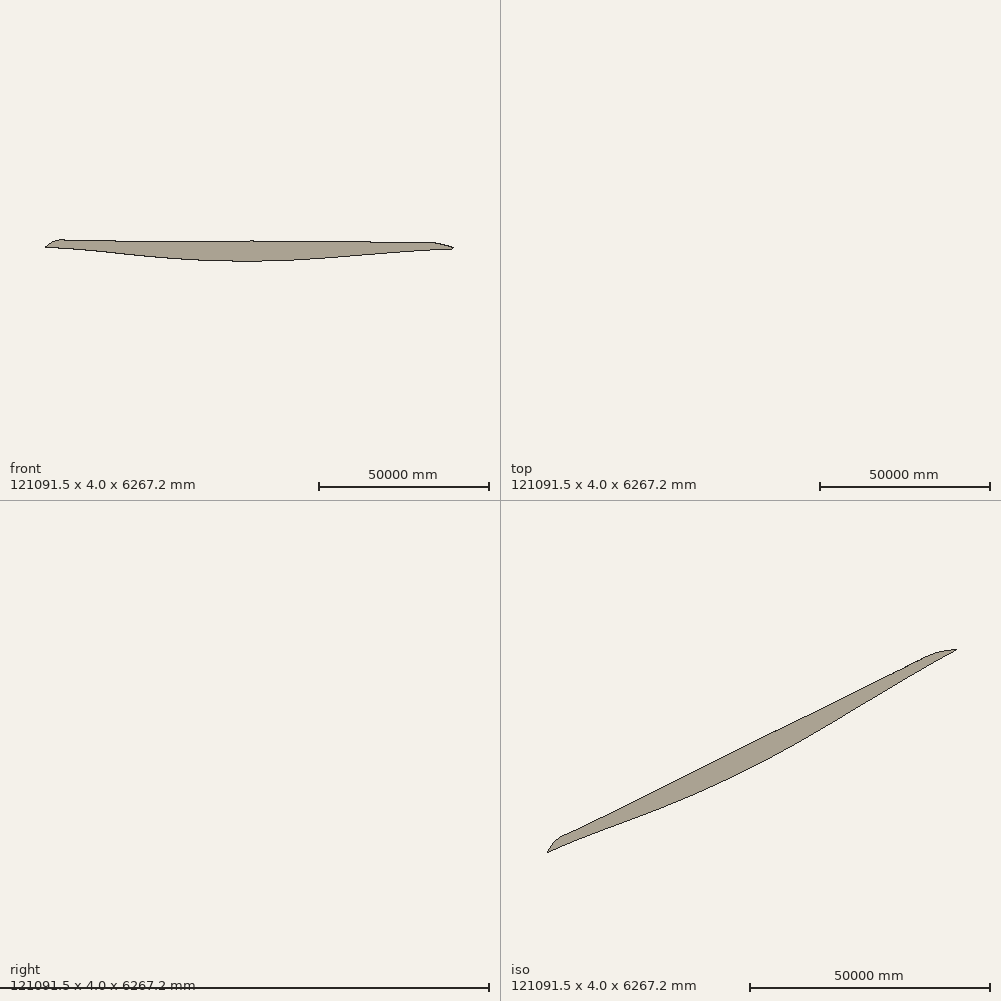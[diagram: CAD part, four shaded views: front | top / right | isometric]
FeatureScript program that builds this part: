
annotation { "Feature Type Name" : "Feature", "Feature Type Description" : "" }
export const myFeature = defineFeature(function(context is Context, id is Id, definition is map)
    precondition{}
    {
        {
            var Q0;
            Q0=qCreatedBy(makeId("Front.planeOp"),FACE);
            var sketch = newSketch(context, id + "F0", { "sketchPlane" : qUnion([Q0])});
            skLineSegment(sketch, "E0", {"start": v(45045.26, 2481.75) * mm, "end": v(45048.8, 2354.8) * mm});
            skLineSegment(sketch, "E1", {"start": v(45048.8, 2354.8) * mm, "end": v(45045.26, 2481.75) * mm});
            skLineSegment(sketch, "E2", {"start": v(45045.26, 2481.75) * mm, "end": v(46150.6, 2484.8) * mm});
            skLineSegment(sketch, "E3", {"start": v(46150.6, 2484.8) * mm, "end": v(46853.03, 2491.6) * mm});
            skLineSegment(sketch, "E4", {"start": v(46853.03, 2491.6) * mm, "end": v(47555.47, 2496.48) * mm});
            skLineSegment(sketch, "E5", {"start": v(47555.47, 2496.48) * mm, "end": v(48440.73, 2492.2) * mm});
            skLineSegment(sketch, "E6", {"start": v(48440.73, 2492.2) * mm, "end": v(49326.03, 2484.26) * mm});
            skLineSegment(sketch, "E7", {"start": v(49326.03, 2484.26) * mm, "end": v(49919.8, 2482.53) * mm});
            skLineSegment(sketch, "E8", {"start": v(49919.8, 2482.53) * mm, "end": v(50513.65, 2486.3) * mm});
            skLineSegment(sketch, "E9", {"start": v(50513.65, 2486.3) * mm, "end": v(51092.21, 2493.99) * mm});
            skLineSegment(sketch, "E10", {"start": v(51092.21, 2493.99) * mm, "end": v(51670.65, 2492.54) * mm});
            skLineSegment(sketch, "E11", {"start": v(51670.65, 2492.54) * mm, "end": v(52134.05, 2476.26) * mm});
            skLineSegment(sketch, "E12", {"start": v(52134.05, 2476.26) * mm, "end": v(52597.09, 2449.36) * mm});
            skLineSegment(sketch, "E13", {"start": v(52597.09, 2449.36) * mm, "end": v(52942.38, 2424.85) * mm});
            skLineSegment(sketch, "E14", {"start": v(52942.38, 2424.85) * mm, "end": v(53287.1, 2394.75) * mm});
            skLineSegment(sketch, "E15", {"start": v(53287.1, 2394.75) * mm, "end": v(53695.08, 2350.15) * mm});
            skLineSegment(sketch, "E16", {"start": v(53695.08, 2350.15) * mm, "end": v(54102.83, 2301.96) * mm});
            skLineSegment(sketch, "E17", {"start": v(54102.83, 2301.96) * mm, "end": v(54430.4, 2263.56) * mm});
            skLineSegment(sketch, "E18", {"start": v(54430.4, 2263.56) * mm, "end": v(54756.52, 2216.5) * mm});
            skLineSegment(sketch, "E19", {"start": v(54756.52, 2216.5) * mm, "end": v(55127.97, 2142.43) * mm});
            skLineSegment(sketch, "E20", {"start": v(55127.97, 2142.43) * mm, "end": v(55497.8, 2058.7) * mm});
            skLineSegment(sketch, "E21", {"start": v(55497.8, 2058.7) * mm, "end": v(55875.09, 1976.62) * mm});
            skLineSegment(sketch, "E22", {"start": v(55875.09, 1976.62) * mm, "end": v(56251.8, 1892.36) * mm});
            skLineSegment(sketch, "E23", {"start": v(56251.8, 1892.36) * mm, "end": v(56457.28, 1842.43) * mm});
            skLineSegment(sketch, "E24", {"start": v(56457.28, 1842.43) * mm, "end": v(56922.02, 1738.62) * mm});
            skLineSegment(sketch, "E25", {"start": v(56922.02, 1738.62) * mm, "end": v(57497.2, 1602.22) * mm});
            skLineSegment(sketch, "E26", {"start": v(57497.2, 1602.22) * mm, "end": v(57794.82, 1520.66) * mm});
            skLineSegment(sketch, "E27", {"start": v(57794.82, 1520.66) * mm, "end": v(58090.22, 1431.35) * mm});
            skLineSegment(sketch, "E28", {"start": v(58090.22, 1431.35) * mm, "end": v(58603.02, 1261.35) * mm});
            skLineSegment(sketch, "E29", {"start": v(58603.02, 1261.35) * mm, "end": v(59086.76, 1091.73) * mm});
            skLineSegment(sketch, "E30", {"start": v(59086.76, 1091.73) * mm, "end": v(59492.98, 946.42) * mm});
            skLineSegment(sketch, "E31", {"start": v(59492.98, 946.42) * mm, "end": v(59938.37, 778.4) * mm});
            skLineSegment(sketch, "E32", {"start": v(59938.37, 778.4) * mm, "end": v(60124.66, 698.72) * mm});
            skLineSegment(sketch, "E33", {"start": v(60124.66, 698.72) * mm, "end": v(60307.18, 610.96) * mm});
            skLineSegment(sketch, "E34", {"start": v(60307.18, 610.96) * mm, "end": v(60545.74, 477.23) * mm});
            skLineSegment(sketch, "E35", {"start": v(60545.74, 477.23) * mm, "end": v(60142.23, 460.8) * mm});
            skLineSegment(sketch, "E36", {"start": v(60142.23, 460.8) * mm, "end": v(59445.87, 431.56) * mm});
            skLineSegment(sketch, "E37", {"start": v(59445.87, 431.56) * mm, "end": v(58749.32, 407.68) * mm});
            skLineSegment(sketch, "E38", {"start": v(58749.32, 407.68) * mm, "end": v(58331.21, 398.44) * mm});
            skLineSegment(sketch, "E39", {"start": v(58331.21, 398.44) * mm, "end": v(57913.16, 387.67) * mm});
            skLineSegment(sketch, "E40", {"start": v(57913.16, 387.67) * mm, "end": v(57073.43, 348.12) * mm});
            skLineSegment(sketch, "E41", {"start": v(57073.43, 348.12) * mm, "end": v(56233.89, 305.57) * mm});
            skLineSegment(sketch, "E42", {"start": v(56233.89, 305.57) * mm, "end": v(55753.85, 287.64) * mm});
            skLineSegment(sketch, "E43", {"start": v(55753.85, 287.64) * mm, "end": v(54874.73, 250.05) * mm});
            skLineSegment(sketch, "E44", {"start": v(54874.73, 250.05) * mm, "end": v(53996, 204.36) * mm});
            skLineSegment(sketch, "E45", {"start": v(53996, 204.36) * mm, "end": v(52751.7, 129.04) * mm});
            skLineSegment(sketch, "E46", {"start": v(52751.7, 129.04) * mm, "end": v(51381.27, 28.51) * mm});
            skLineSegment(sketch, "E47", {"start": v(51381.27, 28.51) * mm, "end": v(50659.65, -10.07) * mm});
            skLineSegment(sketch, "E48", {"start": v(50659.65, -10.07) * mm, "end": v(49938.77, -59.86) * mm});
            skLineSegment(sketch, "E49", {"start": v(49938.77, -59.86) * mm, "end": v(49309.13, -95.03) * mm});
            skLineSegment(sketch, "E50", {"start": v(49309.13, -95.03) * mm, "end": v(48679.37, -128.4) * mm});
            skLineSegment(sketch, "E51", {"start": v(48679.37, -128.4) * mm, "end": v(48018.59, -172.58) * mm});
            skLineSegment(sketch, "E52", {"start": v(48018.59, -172.58) * mm, "end": v(47358.21, -223.25) * mm});
            skLineSegment(sketch, "E53", {"start": v(47358.21, -223.25) * mm, "end": v(46327.99, -299.15) * mm});
            skLineSegment(sketch, "E54", {"start": v(46327.99, -299.15) * mm, "end": v(45952.1, -322.03) * mm});
            skLineSegment(sketch, "E55", {"start": v(45952.1, -322.03) * mm, "end": v(45576.4, -347.4) * mm});
            skLineSegment(sketch, "E56", {"start": v(45576.4, -347.4) * mm, "end": v(45045.26, -395.72) * mm});
            skLineSegment(sketch, "E57", {"start": v(45045.26, -395.72) * mm, "end": v(45033.76, -269.23) * mm});
            skLineSegment(sketch, "E58", {"start": v(45033.76, -269.23) * mm, "end": v(45045.26, -395.72) * mm});
            skLineSegment(sketch, "E59", {"start": v(45045.26, -395.72) * mm, "end": v(43527.08, -510.83) * mm});
            skLineSegment(sketch, "E60", {"start": v(43527.08, -510.83) * mm, "end": v(41972.2, -629.35) * mm});
            skLineSegment(sketch, "E61", {"start": v(41972.2, -629.35) * mm, "end": v(39742.22, -806.31) * mm});
            skLineSegment(sketch, "E62", {"start": v(39742.22, -806.31) * mm, "end": v(37160.87, -1010) * mm});
            skLineSegment(sketch, "E63", {"start": v(37160.87, -1010) * mm, "end": v(34378.68, -1226.8) * mm});
            skLineSegment(sketch, "E64", {"start": v(34378.68, -1226.8) * mm, "end": v(31538.63, -1451.01) * mm});
            skLineSegment(sketch, "E65", {"start": v(31538.63, -1451.01) * mm, "end": v(30380.85, -1549.03) * mm});
            skLineSegment(sketch, "E66", {"start": v(30380.85, -1549.03) * mm, "end": v(29759.62, -1605.47) * mm});
            skLineSegment(sketch, "E67", {"start": v(29759.62, -1605.47) * mm, "end": v(29138.18, -1659.65) * mm});
            skLineSegment(sketch, "E68", {"start": v(29138.18, -1659.65) * mm, "end": v(28532.24, -1706.64) * mm});
            skLineSegment(sketch, "E69", {"start": v(28532.24, -1706.64) * mm, "end": v(27926.32, -1754.06) * mm});
            skLineSegment(sketch, "E70", {"start": v(27926.32, -1754.06) * mm, "end": v(27147.99, -1823.7) * mm});
            skLineSegment(sketch, "E71", {"start": v(27147.99, -1823.7) * mm, "end": v(26369.6, -1892.52) * mm});
            skLineSegment(sketch, "E72", {"start": v(26369.6, -1892.52) * mm, "end": v(25837.45, -1932.75) * mm});
            skLineSegment(sketch, "E73", {"start": v(25837.45, -1932.75) * mm, "end": v(25305.12, -1970.8) * mm});
            skLineSegment(sketch, "E74", {"start": v(25305.12, -1970.8) * mm, "end": v(24325.6, -2049.34) * mm});
            skLineSegment(sketch, "E75", {"start": v(24325.6, -2049.34) * mm, "end": v(23610.6, -2114.97) * mm});
            skLineSegment(sketch, "E76", {"start": v(23610.6, -2114.97) * mm, "end": v(22894.99, -2171.1) * mm});
            skLineSegment(sketch, "E77", {"start": v(22894.99, -2171.1) * mm, "end": v(22494.02, -2192.9) * mm});
            skLineSegment(sketch, "E78", {"start": v(22494.02, -2192.9) * mm, "end": v(22093, -2214.05) * mm});
            skLineSegment(sketch, "E79", {"start": v(22093, -2214.05) * mm, "end": v(21438.48, -2260.84) * mm});
            skLineSegment(sketch, "E80", {"start": v(21438.48, -2260.84) * mm, "end": v(21429.4, -2134.17) * mm});
            skLineSegment(sketch, "E81", {"start": v(21429.4, -2134.17) * mm, "end": v(21438.48, -2260.84) * mm});
            skLineSegment(sketch, "E82", {"start": v(21438.48, -2260.84) * mm, "end": v(20058.11, -2364.78) * mm});
            skLineSegment(sketch, "E83", {"start": v(20058.11, -2364.78) * mm, "end": v(18937.92, -2436.89) * mm});
            skLineSegment(sketch, "E84", {"start": v(18937.92, -2436.89) * mm, "end": v(17817.48, -2505.27) * mm});
            skLineSegment(sketch, "E85", {"start": v(17817.48, -2505.27) * mm, "end": v(16514.46, -2589.67) * mm});
            skLineSegment(sketch, "E86", {"start": v(16514.46, -2589.67) * mm, "end": v(15211.54, -2676.26) * mm});
            skLineSegment(sketch, "E87", {"start": v(15211.54, -2676.26) * mm, "end": v(13451.6, -2785.12) * mm});
            skLineSegment(sketch, "E88", {"start": v(13451.6, -2785.12) * mm, "end": v(11690.44, -2868.87) * mm});
            skLineSegment(sketch, "E89", {"start": v(11690.44, -2868.87) * mm, "end": v(10862.63, -2896.15) * mm});
            skLineSegment(sketch, "E90", {"start": v(10862.63, -2896.15) * mm, "end": v(10034.74, -2922) * mm});
            skLineSegment(sketch, "E91", {"start": v(10034.74, -2922) * mm, "end": v(8682.19, -2973.67) * mm});
            skLineSegment(sketch, "E92", {"start": v(8682.19, -2973.67) * mm, "end": v(7329.74, -3027.67) * mm});
            skLineSegment(sketch, "E93", {"start": v(7329.74, -3027.67) * mm, "end": v(5977.04, -3068.9) * mm});
            skLineSegment(sketch, "E94", {"start": v(5977.04, -3068.9) * mm, "end": v(4581.82, -3088.75) * mm});
            skLineSegment(sketch, "E95", {"start": v(4581.82, -3088.75) * mm, "end": v(3186.37, -3103.26) * mm});
            skLineSegment(sketch, "E96", {"start": v(3186.37, -3103.26) * mm, "end": v(1934.83, -3124.24) * mm});
            skLineSegment(sketch, "E97", {"start": v(1934.83, -3124.24) * mm, "end": v(683.35, -3133.59) * mm});
            skLineSegment(sketch, "E98", {"start": v(683.35, -3133.59) * mm, "end": v(110.99, -3127.46) * mm});
            skLineSegment(sketch, "E99", {"start": v(110.99, -3127.46) * mm, "end": v(-461.33, -3115.55) * mm});
            skLineSegment(sketch, "E100", {"start": v(-461.33, -3115.55) * mm, "end": v(-458.69, -2988.58) * mm});
            skLineSegment(sketch, "E101", {"start": v(-458.69, -2988.58) * mm, "end": v(-461.33, -3115.55) * mm});
            skLineSegment(sketch, "E102", {"start": v(-461.33, -3115.55) * mm, "end": v(-1725, -3125.28) * mm});
            skLineSegment(sketch, "E103", {"start": v(-1725, -3125.28) * mm, "end": v(-2988.68, -3125.86) * mm});
            skLineSegment(sketch, "E104", {"start": v(-2988.68, -3125.86) * mm, "end": v(-4995.94, -3106.18) * mm});
            skLineSegment(sketch, "E105", {"start": v(-4995.94, -3106.18) * mm, "end": v(-7003.17, -3074.17) * mm});
            skLineSegment(sketch, "E106", {"start": v(-7003.17, -3074.17) * mm, "end": v(-8958.57, -3040.4) * mm});
            skLineSegment(sketch, "E107", {"start": v(-8958.57, -3040.4) * mm, "end": v(-10913.3, -2983.88) * mm});
            skLineSegment(sketch, "E108", {"start": v(-10913.3, -2983.88) * mm, "end": v(-12168.67, -2929.14) * mm});
            skLineSegment(sketch, "E109", {"start": v(-12168.67, -2929.14) * mm, "end": v(-13424.34, -2884.74) * mm});
            skLineSegment(sketch, "E110", {"start": v(-13424.34, -2884.74) * mm, "end": v(-13675.25, -2879.61) * mm});
            skLineSegment(sketch, "E111", {"start": v(-13675.25, -2879.61) * mm, "end": v(-13672.65, -2752.64) * mm});
            skLineSegment(sketch, "E112", {"start": v(-13672.65, -2752.64) * mm, "end": v(-13675.25, -2879.61) * mm});
            skLineSegment(sketch, "E113", {"start": v(-13675.25, -2879.61) * mm, "end": v(-15169.3, -2817.5) * mm});
            skLineSegment(sketch, "E114", {"start": v(-15169.3, -2817.5) * mm, "end": v(-16662.74, -2743) * mm});
            skLineSegment(sketch, "E115", {"start": v(-16662.74, -2743) * mm, "end": v(-19323.75, -2576.66) * mm});
            skLineSegment(sketch, "E116", {"start": v(-19323.75, -2576.66) * mm, "end": v(-21983.36, -2387.49) * mm});
            skLineSegment(sketch, "E117", {"start": v(-21983.36, -2387.49) * mm, "end": v(-24420.28, -2211.1) * mm});
            skLineSegment(sketch, "E118", {"start": v(-24420.28, -2211.1) * mm, "end": v(-26856.2, -2022.49) * mm});
            skLineSegment(sketch, "E119", {"start": v(-26856.2, -2022.49) * mm, "end": v(-29261.98, -1812.56) * mm});
            skLineSegment(sketch, "E120", {"start": v(-29261.98, -1812.56) * mm, "end": v(-31666.14, -1583.88) * mm});
            skLineSegment(sketch, "E121", {"start": v(-31666.14, -1583.88) * mm, "end": v(-34017.47, -1349.67) * mm});
            skLineSegment(sketch, "E122", {"start": v(-34017.47, -1349.67) * mm, "end": v(-36368.24, -1109.79) * mm});
            skLineSegment(sketch, "E123", {"start": v(-36368.24, -1109.79) * mm, "end": v(-38171.84, -922.52) * mm});
            skLineSegment(sketch, "E124", {"start": v(-38171.84, -922.52) * mm, "end": v(-39974.33, -725.06) * mm});
            skLineSegment(sketch, "E125", {"start": v(-39974.33, -725.06) * mm, "end": v(-41151.54, -587.06) * mm});
            skLineSegment(sketch, "E126", {"start": v(-41151.54, -587.06) * mm, "end": v(-41136.76, -460.92) * mm});
            skLineSegment(sketch, "E127", {"start": v(-41136.76, -460.92) * mm, "end": v(-41151.54, -587.06) * mm});
            skLineSegment(sketch, "E128", {"start": v(-41151.54, -587.06) * mm, "end": v(-43335.64, -364.3) * mm});
            skLineSegment(sketch, "E129", {"start": v(-43335.64, -364.3) * mm, "end": v(-45116.15, -188.68) * mm});
            skLineSegment(sketch, "E130", {"start": v(-45116.15, -188.68) * mm, "end": v(-46897.2, -18.2) * mm});
            skLineSegment(sketch, "E131", {"start": v(-46897.2, -18.2) * mm, "end": v(-49639, 232.88) * mm});
            skLineSegment(sketch, "E132", {"start": v(-49639, 232.88) * mm, "end": v(-52382.76, 462.09) * mm});
            skLineSegment(sketch, "E133", {"start": v(-52382.76, 462.09) * mm, "end": v(-54561.85, 620.64) * mm});
            skLineSegment(sketch, "E134", {"start": v(-54561.85, 620.64) * mm, "end": v(-56742.88, 748.58) * mm});
            skLineSegment(sketch, "E135", {"start": v(-56742.88, 748.58) * mm, "end": v(-57997.03, 807.12) * mm});
            skLineSegment(sketch, "E136", {"start": v(-57997.03, 807.12) * mm, "end": v(-59251.08, 867.4) * mm});
            skLineSegment(sketch, "E137", {"start": v(-59251.08, 867.4) * mm, "end": v(-60545.74, 942.76) * mm});
            skLineSegment(sketch, "E138", {"start": v(-60545.74, 942.76) * mm, "end": v(-60367.91, 1068.16) * mm});
            skLineSegment(sketch, "E139", {"start": v(-60367.91, 1068.16) * mm, "end": v(-60181.55, 1212.13) * mm});
            skLineSegment(sketch, "E140", {"start": v(-60181.55, 1212.13) * mm, "end": v(-59998.22, 1360.06) * mm});
            skLineSegment(sketch, "E141", {"start": v(-59998.22, 1360.06) * mm, "end": v(-59542.7, 1721.22) * mm});
            skLineSegment(sketch, "E142", {"start": v(-59542.7, 1721.22) * mm, "end": v(-59463.77, 1621.7) * mm});
            skLineSegment(sketch, "E143", {"start": v(-59463.77, 1621.7) * mm, "end": v(-59542.7, 1721.22) * mm});
            skLineSegment(sketch, "E144", {"start": v(-59542.7, 1721.22) * mm, "end": v(-59512.44, 1745.3) * mm});
            skLineSegment(sketch, "E145", {"start": v(-59512.44, 1745.3) * mm, "end": v(-59314.25, 1903.41) * mm});
            skLineSegment(sketch, "E146", {"start": v(-59314.25, 1903.41) * mm, "end": v(-59113.43, 2058.12) * mm});
            skLineSegment(sketch, "E147", {"start": v(-59113.43, 2058.12) * mm, "end": v(-58916, 2198.18) * mm});
            skLineSegment(sketch, "E148", {"start": v(-58916, 2198.18) * mm, "end": v(-58713.03, 2330.26) * mm});
            skLineSegment(sketch, "E149", {"start": v(-58713.03, 2330.26) * mm, "end": v(-58485.19, 2465.7) * mm});
            skLineSegment(sketch, "E150", {"start": v(-58485.19, 2465.7) * mm, "end": v(-58250.85, 2589.34) * mm});
            skLineSegment(sketch, "E151", {"start": v(-58250.85, 2589.34) * mm, "end": v(-58059.59, 2677.53) * mm});
            skLineSegment(sketch, "E152", {"start": v(-58059.59, 2677.53) * mm, "end": v(-57864.1, 2755.86) * mm});
            skLineSegment(sketch, "E153", {"start": v(-57864.1, 2755.86) * mm, "end": v(-57668.73, 2823.04) * mm});
            skLineSegment(sketch, "E154", {"start": v(-57668.73, 2823.04) * mm, "end": v(-57470.76, 2882.28) * mm});
            skLineSegment(sketch, "E155", {"start": v(-57470.76, 2882.28) * mm, "end": v(-57330.15, 2920.17) * mm});
            skLineSegment(sketch, "E156", {"start": v(-57330.15, 2920.17) * mm, "end": v(-57297.13, 2797.54) * mm});
            skLineSegment(sketch, "E157", {"start": v(-57297.13, 2797.54) * mm, "end": v(-57330.15, 2920.17) * mm});
            skLineSegment(sketch, "E158", {"start": v(-57330.15, 2920.17) * mm, "end": v(-57101.14, 2974.84) * mm});
            skLineSegment(sketch, "E159", {"start": v(-57101.14, 2974.84) * mm, "end": v(-56694.26, 3052.69) * mm});
            skLineSegment(sketch, "E160", {"start": v(-56694.26, 3052.69) * mm, "end": v(-56387.45, 3099.17) * mm});
            skLineSegment(sketch, "E161", {"start": v(-56387.45, 3099.17) * mm, "end": v(-56078.87, 3128.1) * mm});
            skLineSegment(sketch, "E162", {"start": v(-56078.87, 3128.1) * mm, "end": v(-56067, 3001.66) * mm});
            skLineSegment(sketch, "E163", {"start": v(-56067, 3001.66) * mm, "end": v(-56078.87, 3128.1) * mm});
            skLineSegment(sketch, "E164", {"start": v(-56078.87, 3128.1) * mm, "end": v(-56073.84, 3128.38) * mm});
            skLineSegment(sketch, "E165", {"start": v(-56073.84, 3128.38) * mm, "end": v(-56062, 3001.94) * mm});
            skLineSegment(sketch, "E166", {"start": v(-56062, 3001.94) * mm, "end": v(-56073.84, 3128.38) * mm});
            skLineSegment(sketch, "E167", {"start": v(-56073.84, 3128.38) * mm, "end": v(-55748.82, 3133.59) * mm});
            skLineSegment(sketch, "E168", {"start": v(-55748.82, 3133.59) * mm, "end": v(-55423.57, 3122.92) * mm});
            skLineSegment(sketch, "E169", {"start": v(-55423.57, 3122.92) * mm, "end": v(-55045.7, 3106.48) * mm});
            skLineSegment(sketch, "E170", {"start": v(-55045.7, 3106.48) * mm, "end": v(-54314.46, 3067.98) * mm});
            skLineSegment(sketch, "E171", {"start": v(-54314.46, 3067.98) * mm, "end": v(-53518.12, 3026.96) * mm});
            skLineSegment(sketch, "E172", {"start": v(-53518.12, 3026.96) * mm, "end": v(-52496.55, 2988.32) * mm});
            skLineSegment(sketch, "E173", {"start": v(-52496.55, 2988.32) * mm, "end": v(-51844.26, 2964.65) * mm});
            skLineSegment(sketch, "E174", {"start": v(-51844.26, 2964.65) * mm, "end": v(-51191.83, 2947.68) * mm});
            skLineSegment(sketch, "E175", {"start": v(-51191.83, 2947.68) * mm, "end": v(-50425.13, 2943.42) * mm});
            skLineSegment(sketch, "E176", {"start": v(-50425.13, 2943.42) * mm, "end": v(-49658.4, 2939.07) * mm});
            skLineSegment(sketch, "E177", {"start": v(-49658.4, 2939.07) * mm, "end": v(-48900.88, 2919.36) * mm});
            skLineSegment(sketch, "E178", {"start": v(-48900.88, 2919.36) * mm, "end": v(-48143.35, 2899.04) * mm});
            skLineSegment(sketch, "E179", {"start": v(-48143.35, 2899.04) * mm, "end": v(-47527.3, 2893.1) * mm});
            skLineSegment(sketch, "E180", {"start": v(-47527.3, 2893.1) * mm, "end": v(-46911.25, 2887.46) * mm});
            skLineSegment(sketch, "E181", {"start": v(-46911.25, 2887.46) * mm, "end": v(-46219.48, 2870.8) * mm});
            skLineSegment(sketch, "E182", {"start": v(-46219.48, 2870.8) * mm, "end": v(-45527.7, 2857.03) * mm});
            skLineSegment(sketch, "E183", {"start": v(-45527.7, 2857.03) * mm, "end": v(-44962.56, 2857.26) * mm});
            skLineSegment(sketch, "E184", {"start": v(-44962.56, 2857.26) * mm, "end": v(-44397.43, 2855.46) * mm});
            skLineSegment(sketch, "E185", {"start": v(-44397.43, 2855.46) * mm, "end": v(-43989.46, 2846.31) * mm});
            skLineSegment(sketch, "E186", {"start": v(-43989.46, 2846.31) * mm, "end": v(-43581.46, 2840.04) * mm});
            skLineSegment(sketch, "E187", {"start": v(-43581.46, 2840.04) * mm, "end": v(-43217.25, 2843.72) * mm});
            skLineSegment(sketch, "E188", {"start": v(-43217.25, 2843.72) * mm, "end": v(-42853.04, 2846.74) * mm});
            skLineSegment(sketch, "E189", {"start": v(-42853.04, 2846.74) * mm, "end": v(-42434.12, 2838.03) * mm});
            skLineSegment(sketch, "E190", {"start": v(-42434.12, 2838.03) * mm, "end": v(-42015.22, 2825.97) * mm});
            skLineSegment(sketch, "E191", {"start": v(-42015.22, 2825.97) * mm, "end": v(-41558.12, 2822.46) * mm});
            skLineSegment(sketch, "E192", {"start": v(-41558.12, 2822.46) * mm, "end": v(-41101.02, 2827.06) * mm});
            skLineSegment(sketch, "E193", {"start": v(-41101.02, 2827.06) * mm, "end": v(-41099.75, 2700.06) * mm});
            skLineSegment(sketch, "E194", {"start": v(-41099.75, 2700.06) * mm, "end": v(-41101.02, 2827.06) * mm});
            skLineSegment(sketch, "E195", {"start": v(-41101.02, 2827.06) * mm, "end": v(-40249.84, 2810.62) * mm});
            skLineSegment(sketch, "E196", {"start": v(-40249.84, 2810.62) * mm, "end": v(-39398.56, 2800.72) * mm});
            skLineSegment(sketch, "E197", {"start": v(-39398.56, 2800.72) * mm, "end": v(-38213, 2799.5) * mm});
            skLineSegment(sketch, "E198", {"start": v(-38213, 2799.5) * mm, "end": v(-37027.4, 2801.02) * mm});
            skLineSegment(sketch, "E199", {"start": v(-37027.4, 2801.02) * mm, "end": v(-35751.02, 2793.4) * mm});
            skLineSegment(sketch, "E200", {"start": v(-35751.02, 2793.4) * mm, "end": v(-34474.67, 2785.07) * mm});
            skLineSegment(sketch, "E201", {"start": v(-34474.67, 2785.07) * mm, "end": v(-32996.21, 2787.15) * mm});
            skLineSegment(sketch, "E202", {"start": v(-32996.21, 2787.15) * mm, "end": v(-31517.76, 2792.74) * mm});
            skLineSegment(sketch, "E203", {"start": v(-31517.76, 2792.74) * mm, "end": v(-29221.37, 2789.42) * mm});
            skLineSegment(sketch, "E204", {"start": v(-29221.37, 2789.42) * mm, "end": v(-27316.01, 2788.37) * mm});
            skLineSegment(sketch, "E205", {"start": v(-27316.01, 2788.37) * mm, "end": v(-25410.66, 2786.85) * mm});
            skLineSegment(sketch, "E206", {"start": v(-25410.66, 2786.85) * mm, "end": v(-23953.08, 2782.5) * mm});
            skLineSegment(sketch, "E207", {"start": v(-23953.08, 2782.5) * mm, "end": v(-22495.47, 2782.33) * mm});
            skLineSegment(sketch, "E208", {"start": v(-22495.47, 2782.33) * mm, "end": v(-21044.12, 2790.53) * mm});
            skLineSegment(sketch, "E209", {"start": v(-21044.12, 2790.53) * mm, "end": v(-19592.76, 2792.49) * mm});
            skLineSegment(sketch, "E210", {"start": v(-19592.76, 2792.49) * mm, "end": v(-18589.33, 2783.47) * mm});
            skLineSegment(sketch, "E211", {"start": v(-18589.33, 2783.47) * mm, "end": v(-17585.93, 2776.8) * mm});
            skLineSegment(sketch, "E212", {"start": v(-17585.93, 2776.8) * mm, "end": v(-16394.95, 2784.03) * mm});
            skLineSegment(sketch, "E213", {"start": v(-16394.95, 2784.03) * mm, "end": v(-15203.97, 2791.4) * mm});
            skLineSegment(sketch, "E214", {"start": v(-15203.97, 2791.4) * mm, "end": v(-14439.58, 2786.85) * mm});
            skLineSegment(sketch, "E215", {"start": v(-14439.58, 2786.85) * mm, "end": v(-13675.25, 2776.26) * mm});
            skLineSegment(sketch, "E216", {"start": v(-13675.25, 2776.26) * mm, "end": v(-13677, 2649.26) * mm});
            skLineSegment(sketch, "E217", {"start": v(-13677, 2649.26) * mm, "end": v(-13675.25, 2776.26) * mm});
            skLineSegment(sketch, "E218", {"start": v(-13675.25, 2776.26) * mm, "end": v(-12642.89, 2762.82) * mm});
            skLineSegment(sketch, "E219", {"start": v(-12642.89, 2762.82) * mm, "end": v(-11610.45, 2760.84) * mm});
            skLineSegment(sketch, "E220", {"start": v(-11610.45, 2760.84) * mm, "end": v(-10404.77, 2775.12) * mm});
            skLineSegment(sketch, "E221", {"start": v(-10404.77, 2775.12) * mm, "end": v(-9199.08, 2792.64) * mm});
            skLineSegment(sketch, "E222", {"start": v(-9199.08, 2792.64) * mm, "end": v(-8054.56, 2798.53) * mm});
            skLineSegment(sketch, "E223", {"start": v(-8054.56, 2798.53) * mm, "end": v(-6909.96, 2795.3) * mm});
            skLineSegment(sketch, "E224", {"start": v(-6909.96, 2795.3) * mm, "end": v(-5880.19, 2789.77) * mm});
            skLineSegment(sketch, "E225", {"start": v(-5880.19, 2789.77) * mm, "end": v(-4850.45, 2790.13) * mm});
            skLineSegment(sketch, "E226", {"start": v(-4850.45, 2790.13) * mm, "end": v(-4228.86, 2795.8) * mm});
            skLineSegment(sketch, "E227", {"start": v(-4228.86, 2795.8) * mm, "end": v(-3607.3, 2801.33) * mm});
            skLineSegment(sketch, "E228", {"start": v(-3607.3, 2801.33) * mm, "end": v(-2814.03, 2802.32) * mm});
            skLineSegment(sketch, "E229", {"start": v(-2814.03, 2802.32) * mm, "end": v(-2020.76, 2800.36) * mm});
            skLineSegment(sketch, "E230", {"start": v(-2020.76, 2800.36) * mm, "end": v(-461.33, 2801.66) * mm});
            skLineSegment(sketch, "E231", {"start": v(-461.33, 2801.66) * mm, "end": v(-461.23, 2674.66) * mm});
            skLineSegment(sketch, "E232", {"start": v(-461.23, 2674.66) * mm, "end": v(-461.33, 2801.66) * mm});
            skLineSegment(sketch, "E233", {"start": v(-461.33, 2801.66) * mm, "end": v(646.82, 2808.57) * mm});
            skLineSegment(sketch, "E234", {"start": v(646.82, 2808.57) * mm, "end": v(1754.92, 2798.43) * mm});
            skLineSegment(sketch, "E235", {"start": v(1754.92, 2798.43) * mm, "end": v(2543.77, 2779.18) * mm});
            skLineSegment(sketch, "E236", {"start": v(2543.77, 2779.18) * mm, "end": v(3332.62, 2761.27) * mm});
            skLineSegment(sketch, "E237", {"start": v(3332.62, 2761.27) * mm, "end": v(4288.75, 2754.7) * mm});
            skLineSegment(sketch, "E238", {"start": v(4288.75, 2754.7) * mm, "end": v(5245.01, 2754.08) * mm});
            skLineSegment(sketch, "E239", {"start": v(5245.01, 2754.08) * mm, "end": v(6142.27, 2746.57) * mm});
            skLineSegment(sketch, "E240", {"start": v(6142.27, 2746.57) * mm, "end": v(7039.42, 2731.48) * mm});
            skLineSegment(sketch, "E241", {"start": v(7039.42, 2731.48) * mm, "end": v(8160.55, 2706.26) * mm});
            skLineSegment(sketch, "E242", {"start": v(8160.55, 2706.26) * mm, "end": v(9281.68, 2683.85) * mm});
            skLineSegment(sketch, "E243", {"start": v(9281.68, 2683.85) * mm, "end": v(10555.62, 2671.43) * mm});
            skLineSegment(sketch, "E244", {"start": v(10555.62, 2671.43) * mm, "end": v(11829.66, 2664.12) * mm});
            skLineSegment(sketch, "E245", {"start": v(11829.66, 2664.12) * mm, "end": v(12977.56, 2652.69) * mm});
            skLineSegment(sketch, "E246", {"start": v(12977.56, 2652.69) * mm, "end": v(14125.4, 2636.13) * mm});
            skLineSegment(sketch, "E247", {"start": v(14125.4, 2636.13) * mm, "end": v(16186.98, 2602.52) * mm});
            skLineSegment(sketch, "E248", {"start": v(16186.98, 2602.52) * mm, "end": v(17783.24, 2589.31) * mm});
            skLineSegment(sketch, "E249", {"start": v(17783.24, 2589.31) * mm, "end": v(18859.13, 2590.97) * mm});
            skLineSegment(sketch, "E250", {"start": v(18859.13, 2590.97) * mm, "end": v(19934.97, 2586.44) * mm});
            skLineSegment(sketch, "E251", {"start": v(19934.97, 2586.44) * mm, "end": v(20686.81, 2571.38) * mm});
            skLineSegment(sketch, "E252", {"start": v(20686.81, 2571.38) * mm, "end": v(21438.48, 2547.66) * mm});
            skLineSegment(sketch, "E253", {"start": v(21438.48, 2547.66) * mm, "end": v(21434.46, 2420.7) * mm});
            skLineSegment(sketch, "E254", {"start": v(21434.46, 2420.7) * mm, "end": v(21438.48, 2547.66) * mm});
            skLineSegment(sketch, "E255", {"start": v(21438.48, 2547.66) * mm, "end": v(22172.16, 2535.36) * mm});
            skLineSegment(sketch, "E256", {"start": v(22172.16, 2535.36) * mm, "end": v(22998.93, 2535.24) * mm});
            skLineSegment(sketch, "E257", {"start": v(22998.93, 2535.24) * mm, "end": v(23825.72, 2542.43) * mm});
            skLineSegment(sketch, "E258", {"start": v(23825.72, 2542.43) * mm, "end": v(24543.83, 2546.74) * mm});
            skLineSegment(sketch, "E259", {"start": v(24543.83, 2546.74) * mm, "end": v(25261.91, 2543.42) * mm});
            skLineSegment(sketch, "E260", {"start": v(25261.91, 2543.42) * mm, "end": v(25930.42, 2531.94) * mm});
            skLineSegment(sketch, "E261", {"start": v(25930.42, 2531.94) * mm, "end": v(26598.9, 2523.73) * mm});
            skLineSegment(sketch, "E262", {"start": v(26598.9, 2523.73) * mm, "end": v(27304.02, 2528.91) * mm});
            skLineSegment(sketch, "E263", {"start": v(27304.02, 2528.91) * mm, "end": v(28009.18, 2536.84) * mm});
            skLineSegment(sketch, "E264", {"start": v(28009.18, 2536.84) * mm, "end": v(28886.4, 2533.1) * mm});
            skLineSegment(sketch, "E265", {"start": v(28886.4, 2533.1) * mm, "end": v(29763.58, 2524.57) * mm});
            skLineSegment(sketch, "E266", {"start": v(29763.58, 2524.57) * mm, "end": v(30768.79, 2524.5) * mm});
            skLineSegment(sketch, "E267", {"start": v(30768.79, 2524.5) * mm, "end": v(31774, 2527) * mm});
            skLineSegment(sketch, "E268", {"start": v(31774, 2527) * mm, "end": v(32740.84, 2522.41) * mm});
            skLineSegment(sketch, "E269", {"start": v(32740.84, 2522.41) * mm, "end": v(33707.72, 2515.37) * mm});
            skLineSegment(sketch, "E270", {"start": v(33707.72, 2515.37) * mm, "end": v(35568.5, 2509.69) * mm});
            skLineSegment(sketch, "E271", {"start": v(35568.5, 2509.69) * mm, "end": v(37301.54, 2500.52) * mm});
            skLineSegment(sketch, "E272", {"start": v(37301.54, 2500.52) * mm, "end": v(38950.73, 2490.74) * mm});
            skLineSegment(sketch, "E273", {"start": v(38950.73, 2490.74) * mm, "end": v(40396.6, 2489.24) * mm});
            skLineSegment(sketch, "E274", {"start": v(40396.6, 2489.24) * mm, "end": v(41623.17, 2482.33) * mm});
            skLineSegment(sketch, "E275", {"start": v(41623.17, 2482.33) * mm, "end": v(42631.58, 2486.16) * mm});
            skLineSegment(sketch, "E276", {"start": v(42631.58, 2486.16) * mm, "end": v(43130.66, 2488.7) * mm});
            skLineSegment(sketch, "E277", {"start": v(43130.66, 2488.7) * mm, "end": v(43629.7, 2485.4) * mm});
            skLineSegment(sketch, "E278", {"start": v(43629.7, 2485.4) * mm, "end": v(44040.39, 2476.41) * mm});
            skLineSegment(sketch, "E279", {"start": v(44040.39, 2476.41) * mm, "end": v(44451.1, 2470.5) * mm});
            skLineSegment(sketch, "E280", {"start": v(44451.1, 2470.5) * mm, "end": v(44748.2, 2473.46) * mm});
            skLineSegment(sketch, "E281", {"start": v(44748.2, 2473.46) * mm, "end": v(45045.26, 2481.75) * mm});
            skSolve(sketch);
        }
        {
            var Q0;
            Q0 = qSketchRegion(id + "F0", true);
            extrude(context, id + "F1", {"entities" : qUnion([Q0]), "depth" : 4 * mm, "offsetDistance" : 25 * mm});
        }
    });
